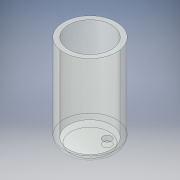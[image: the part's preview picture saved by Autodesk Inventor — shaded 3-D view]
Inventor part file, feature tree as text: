
AUTODESK INVENTOR PART (.ipt)
format: ipt  version: 2018 (Build 220112000, 112)  size: 123,904 bytes
history: native  units: in
note: dims shown in document units (in); Inventor stores cm internally (conversion verified against a paired STEP export)
features: extrude x2, sketch x2, shell x1, fillet x1
ambient origin geometry x8: Origin, YZ Plane, XZ Plane, XY Plane, X Axis, Y Axis, Z Axis, Center Point
bodies: Solid1 (feature_tree)
feature tree (6):
  extrude  "Extrusion1"  Depth=0.8in TaperAngle=0.0deg
  shell  "Shell1"  Thickness=0.043in
  fillet  "Fillet1"  Radius=0.0625in
  extrude  "Extrusion2"  Depth=0.8in TaperAngle=0.0deg
  sketch  "Sketch1"  dims[d0=0.46in d1=0.8in d2=0.0in d3=0.043in d4=0.0625in]
  sketch  "Sketch2"  dims[d5=0.075in d6=0.8in d7=0.0in]
